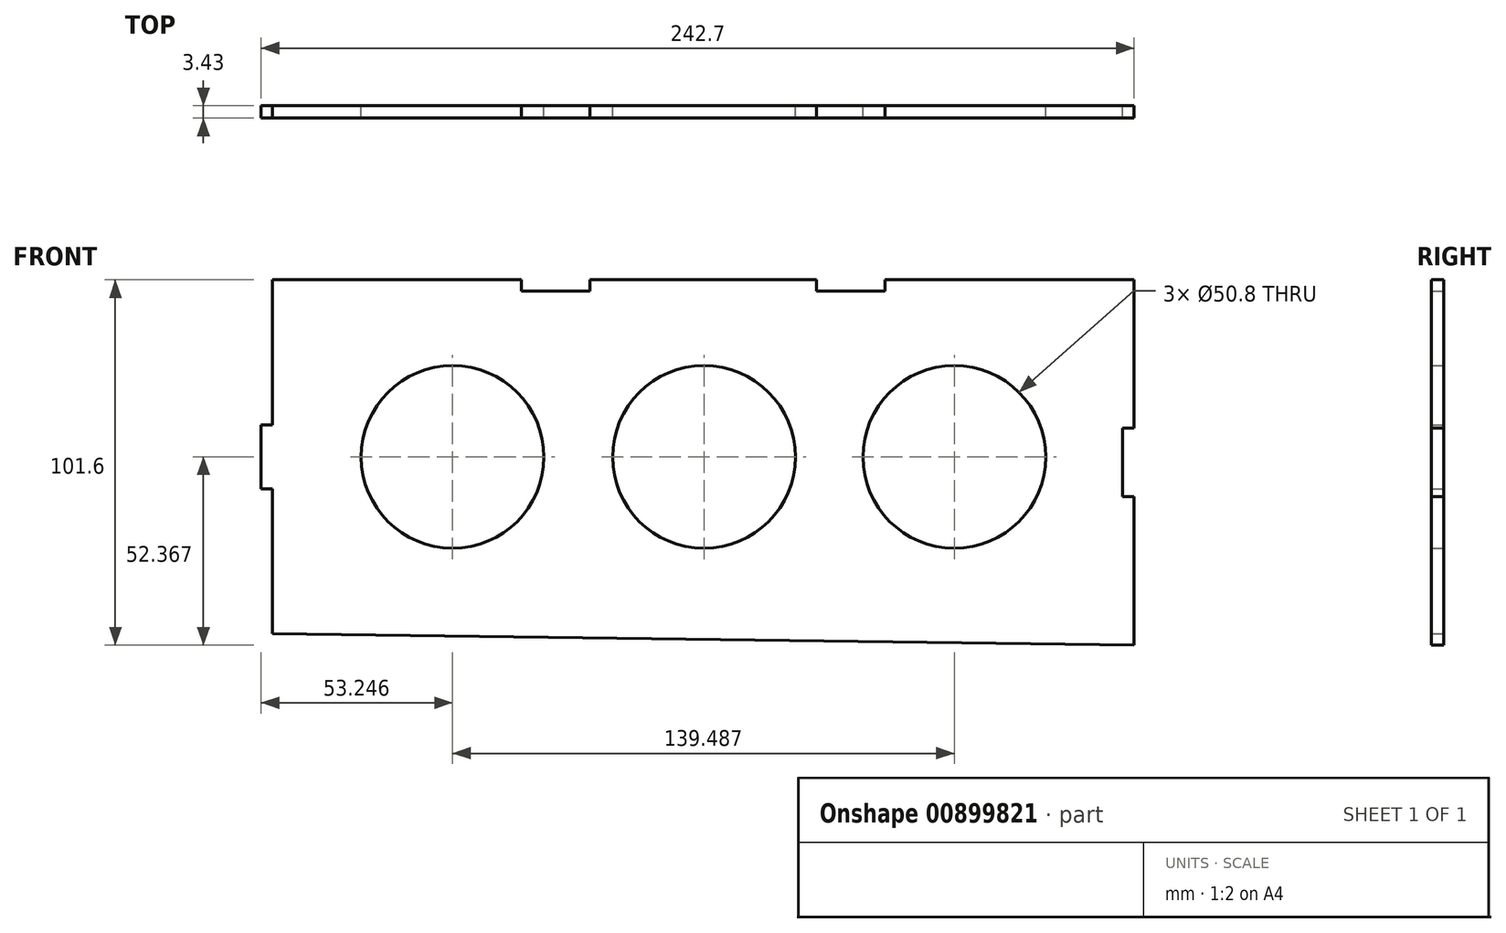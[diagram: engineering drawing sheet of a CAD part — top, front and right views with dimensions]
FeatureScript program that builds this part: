
annotation { "Feature Type Name" : "Feature", "Feature Type Description" : "" }
export const myFeature = defineFeature(function(context is Context, id is Id, definition is map)
    precondition{}
    {
        {
            var Q0;
            Q0=qCreatedBy(makeId("Front.planeOp"),FACE);
            var sketch = newSketch(context, id + "F0", { "sketchPlane" : qUnion([Q0])});
            skLineSegment(sketch, "E0", {"start": v(644.35, -71.7) * mm, "end": v(647.53, -71.7) * mm});
            skLineSegment(sketch, "E1", {"start": v(644.35, -53.91) * mm, "end": v(644.35, -71.7) * mm});
            skLineSegment(sketch, "E2", {"start": v(647.53, -53.91) * mm, "end": v(644.35, -53.91) * mm});
            skLineSegment(sketch, "E3", {"start": v(716.74, -13.59) * mm, "end": v(716.74, -16.76) * mm});
            skLineSegment(sketch, "E4", {"start": v(716.74, -16.76) * mm, "end": v(735.8, -16.76) * mm});
            skLineSegment(sketch, "E5", {"start": v(735.8, -16.76) * mm, "end": v(735.8, -13.59) * mm});
            skLineSegment(sketch, "E6", {"start": v(798.79, -13.59) * mm, "end": v(798.79, -16.76) * mm});
            skLineSegment(sketch, "E7", {"start": v(798.79, -16.76) * mm, "end": v(817.84, -16.76) * mm});
            skLineSegment(sketch, "E8", {"start": v(817.84, -16.76) * mm, "end": v(817.84, -13.59) * mm});
            skLineSegment(sketch, "E9", {"start": v(887.05, -54.86) * mm, "end": v(883.88, -54.86) * mm});
            skLineSegment(sketch, "E10", {"start": v(883.88, -54.86) * mm, "end": v(883.88, -73.91) * mm});
            skLineSegment(sketch, "E11", {"start": v(883.88, -73.91) * mm, "end": v(887.05, -73.91) * mm});
            skCircle(sketch, "E12", {"center": v(697.6, -62.82) * mm, "radius": 25.4 * mm});
            skCircle(sketch, "E13", {"center": v(767.48, -62.82) * mm, "radius": 25.4 * mm});
            skCircle(sketch, "E14", {"center": v(837.08, -62.82) * mm, "radius": 25.4 * mm});
            skLineSegment(sketch, "E15", {"start": v(887.05, -54.86) * mm, "end": v(887.05, -13.59) * mm});
            skLineSegment(sketch, "E16", {"start": v(647.53, -112.01) * mm, "end": v(887.05, -115.19) * mm});
            skLineSegment(sketch, "E17", {"start": v(647.53, -71.7) * mm, "end": v(647.53, -112.01) * mm});
            skLineSegment(sketch, "E18", {"start": v(716.74, -13.59) * mm, "end": v(647.53, -13.59) * mm});
            skLineSegment(sketch, "E19", {"start": v(647.53, -13.59) * mm, "end": v(647.53, -53.91) * mm});
            skLineSegment(sketch, "E20", {"start": v(798.79, -13.59) * mm, "end": v(735.8, -13.59) * mm});
            skLineSegment(sketch, "E21", {"start": v(887.05, -13.59) * mm, "end": v(817.84, -13.59) * mm});
            skLineSegment(sketch, "E22", {"start": v(887.05, -115.19) * mm, "end": v(887.05, -73.91) * mm});
            skSolve(sketch);
        }
        {
            var Q0;
            Q0 = qSketchRegion(id + "F0", true);
            extrude(context, id + "F1", {"entities" : qUnion([Q0]), "depth" : 3.43 * mm, "offsetDistance" : 25.4 * mm});
        }
    });
